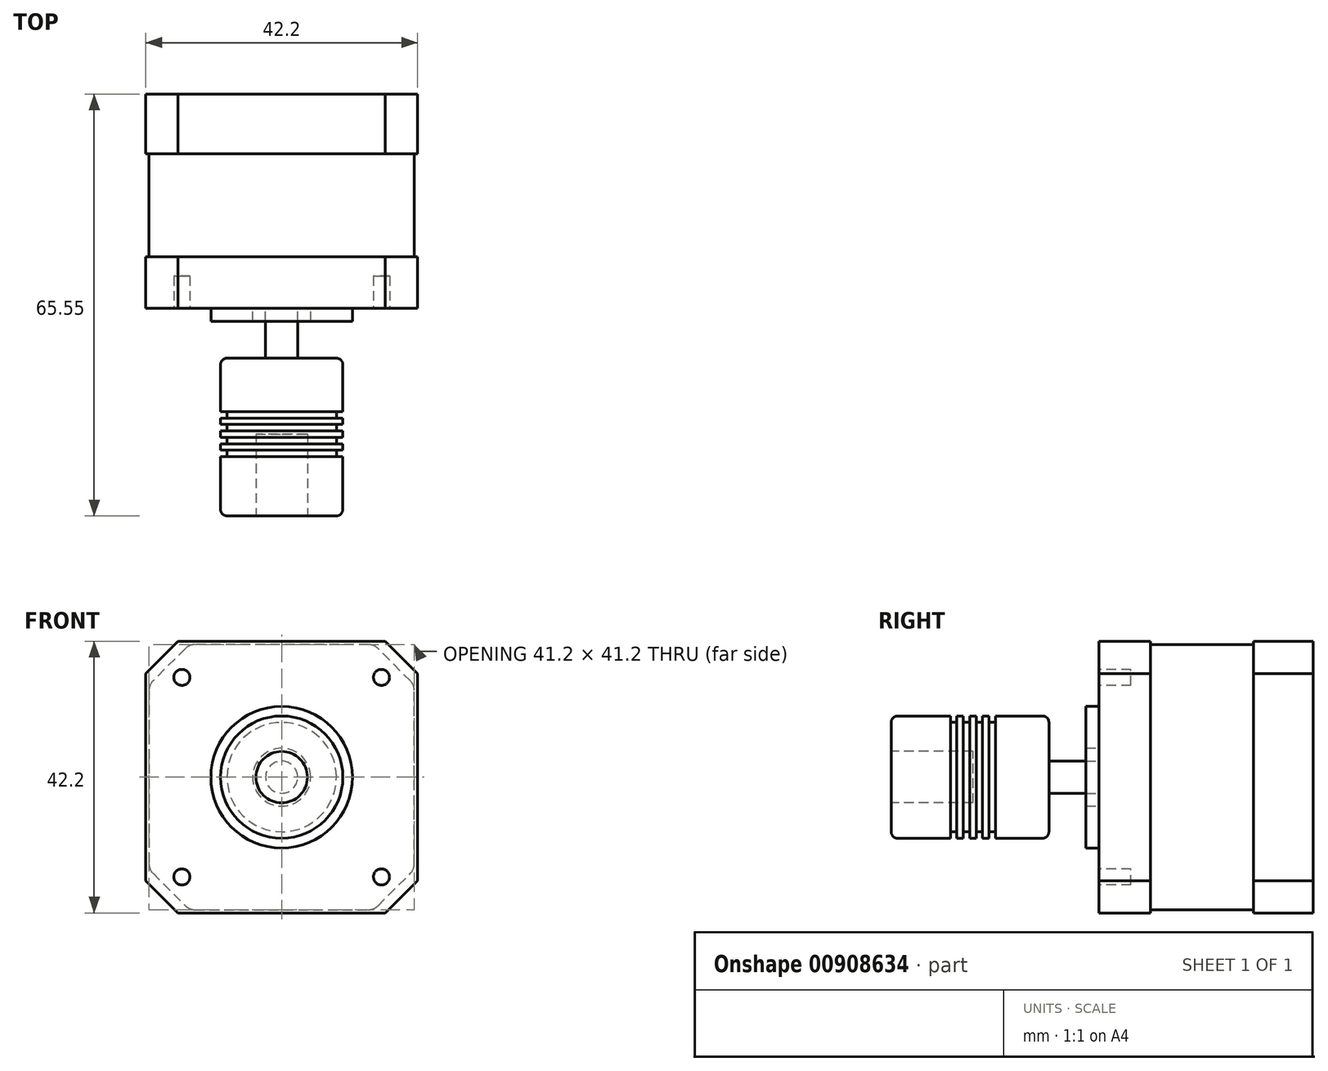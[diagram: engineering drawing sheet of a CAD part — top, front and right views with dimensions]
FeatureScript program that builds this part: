
annotation { "Feature Type Name" : "Feature", "Feature Type Description" : "" }
export const myFeature = defineFeature(function(context is Context, id is Id, definition is map)
    precondition{}
    {
        {
            var Q0;
            Q0=qCreatedBy(makeId("Front.planeOp"),FACE);
            var sketch = newSketch(context, id + "F0", { "sketchPlane" : qUnion([Q0])});
            skLineSegment(sketch, "E0.bottom", {"start": v(-21.1, 21.1) * mm, "end": v(21.1, 21.1) * mm});
            skLineSegment(sketch, "E0.top", {"start": v(-21.1, -21.1) * mm, "end": v(21.1, -21.1) * mm});
            skLineSegment(sketch, "E0.left", {"start": v(-21.1, 21.1) * mm, "end": v(-21.1, -21.1) * mm});
            skLineSegment(sketch, "E0.right", {"start": v(21.1, 21.1) * mm, "end": v(21.1, -21.1) * mm});
            skLineSegment(sketch, "E1", {"start": v(-21.1, 21.1) * mm, "end": v(21.1, -21.1) * mm, "construction": true});
            skCircle(sketch, "E2", {"center": v(0, 0) * mm, "radius": 2.5 * mm});
            skSolve(sketch);
        }
        {
            var Q0;
            Q0=makeQuery(id+"F0.imprint","IMPRINT",FACE,{"disambiguationData":[TD([[makeQuery(id+"F0.imprint","IMPRINT",EDGE,{"derivedFrom":sQuery(id+"F0.wireOp",EDGE,"E2")}),1.0]])]});
            var Q1;
            Q1=makeQuery(id+"F0.imprint","IMPRINT",FACE,{"disambiguationData":[TD([[makeQuery(id+"F0.imprint","IMPRINT",EDGE,{"derivedFrom":sQuery(id+"F0.wireOp",EDGE,"E0.bottom")}),-1.0]])]});
            extrude(context, id + "F1", {"entities" : qUnion([Q0, Q1]), "oppositeDirection" : true, "depth" : 33.3 * mm, "offsetDistance" : 25 * mm});
        }
        {
            var Q0;
            Q0=makeQuery(id+"F1.opExtrude","SWEPT_EDGE",EDGE,{"disambiguationData":[OSD([sQuery(id+"F0.wireOp",EDGE,"E0.bottom"),sQuery(id+"F0.wireOp",EDGE,"E0.right")])]});
            var Q1;
            Q1=makeQuery(id+"F1.opExtrude","SWEPT_EDGE",EDGE,{"disambiguationData":[OSD([sQuery(id+"F0.wireOp",EDGE,"E0.bottom"),sQuery(id+"F0.wireOp",EDGE,"E0.left")])]});
            var Q2;
            Q2=makeQuery(id+"F1.opExtrude","SWEPT_EDGE",EDGE,{"disambiguationData":[OSD([sQuery(id+"F0.wireOp",EDGE,"E0.top"),sQuery(id+"F0.wireOp",EDGE,"E0.right")])]});
            var Q3;
            Q3=makeQuery(id+"F1.opExtrude","SWEPT_EDGE",EDGE,{"disambiguationData":[OSD([sQuery(id+"F0.wireOp",EDGE,"E0.top"),sQuery(id+"F0.wireOp",EDGE,"E0.left")])]});
            chamfer(context, id + "F2", {"entities" : qUnion([Q0, Q1, Q2, Q3]), "width" : 5 * mm, "tangentPropagation" : true});
        }
        {
            var Q0;
            Q0=makeQuery(id+"F0.imprint","IMPRINT",FACE,{"disambiguationData":[TD([[makeQuery(id+"F0.imprint","IMPRINT",EDGE,{"derivedFrom":sQuery(id+"F0.wireOp",EDGE,"E2")}),1.0]])]});
            extrude(context, id + "F3", {"entities" : qUnion([Q0]), "operationType" : NewBodyOperationType.ADD, "depth" : 20 * mm, "offsetDistance" : 25 * mm});
        }
        {
            var Q0;
            Q0=makeQuery(id+"F1.opExtrude","CAP_FACE",FACE,{"disambiguationData":[OSD([sQuery(id+"F0.wireOp",EDGE,"E0.bottom"),sQuery(id+"F0.wireOp",EDGE,"E0.top"),sQuery(id+"F0.wireOp",EDGE,"E0.left"),sQuery(id+"F0.wireOp",EDGE,"E0.right")])],"isStart":true});
            var sketch = newSketch(context, id + "F4", { "sketchPlane" : qUnion([Q0])});
            skCircle(sketch, "E3", {"center": v(0, 0) * mm, "radius": 4.5 * mm});
            skCircle(sketch, "E4", {"center": v(0, 0) * mm, "radius": 11 * mm});
            skSolve(sketch);
        }
        {
            var Q0;
            Q0 = qSketchRegion(id + "F4", true);
            extrude(context, id + "F5", {"entities" : qUnion([Q0]), "operationType" : NewBodyOperationType.ADD, "depth" : 2 * mm, "offsetDistance" : 25 * mm});
        }
        {
            var Q0;
            {var subQ0=sQuery(id+"F0.wireOp",EDGE,"E0.left");var subQ1=sQuery(id+"F0.wireOp",EDGE,"E0.bottom");var subQ2=sQuery(id+"F0.wireOp",EDGE,"E0.top");var subQ3=sQuery(id+"F0.wireOp",EDGE,"E0.right");Q0=makeQuery(id+"F5.boolean.opBoolean","SPLIT",FACE,{"disambiguationData":[TD([makeQuery(id+"F1.opExtrude","SWEPT_FACE",FACE,{"disambiguationData":[OSD([subQ1])]})])],"derivedFrom":makeQuery(id+"F1.opExtrude","CAP_FACE",FACE,{"disambiguationData":[OSD([subQ1,subQ2,subQ0,subQ3])],"isStart":true})});}
            var sketch = newSketch(context, id + "F6", { "sketchPlane" : qUnion([Q0])});
            skCircle(sketch, "E5", {"center": v(-15.5, 15.5) * mm, "radius": 1.25 * mm});
            skCircle(sketch, "E6.1.0", {"center": v(-15.5, -15.5) * mm, "radius": 1.25 * mm});
            skCircle(sketch, "E6.2.0", {"center": v(15.5, -15.5) * mm, "radius": 1.25 * mm});
            skCircle(sketch, "E6.3.0", {"center": v(15.5, 15.5) * mm, "radius": 1.25 * mm});
            skPoint(sketch, "E6.center", {"position": v(0, 0) * mm});
            skSolve(sketch);
        }
        {
            var Q0;
            Q0 = qSketchRegion(id + "F6", true);
            extrude(context, id + "F7", {"entities" : qUnion([Q0]), "operationType" : NewBodyOperationType.REMOVE, "oppositeDirection" : true, "depth" : 5 * mm, "offsetDistance" : 25 * mm});
        }
        {
            var Q0;
            {var subQ0=sQuery(id+"F0.wireOp",EDGE,"E0.left");var subQ1=sQuery(id+"F0.wireOp",EDGE,"E0.bottom");var subQ2=sQuery(id+"F0.wireOp",EDGE,"E0.top");var subQ3=sQuery(id+"F0.wireOp",EDGE,"E0.right");Q0=makeQuery(id+"F5.boolean.opBoolean","SPLIT",FACE,{"disambiguationData":[TD([makeQuery(id+"F1.opExtrude","SWEPT_FACE",FACE,{"disambiguationData":[OSD([subQ1])]})])],"derivedFrom":makeQuery(id+"F1.opExtrude","CAP_FACE",FACE,{"disambiguationData":[OSD([subQ1,subQ2,subQ0,subQ3])],"isStart":true})});}
            cPlane(context, id + "F8", {"entities" : qUnion([Q0]), "cplaneType" : CPlaneType.OFFSET, "offset" : 8 * mm, "oppositeDirection" : true, "width" : 150 * mm, "height" : 150 * mm});
        }
        {
            var Q0;
            Q0=qCreatedBy(id+"F8.planeOp",FACE);
            var sketch = newSketch(context, id + "F9", { "sketchPlane" : qUnion([Q0])});
            skLineSegment(sketch, "E7", {"start": v(0, 0) * mm, "end": v(0, 20.6) * mm});
            skLineSegment(sketch, "E8", {"start": v(0, 20.6) * mm, "end": v(-14.34, 20.6) * mm});
            skLineSegment(sketch, "E9", {"start": v(-14.34, 20.6) * mm, "end": v(-20.6, 14.34) * mm});
            skLineSegment(sketch, "E10", {"start": v(-20.6, 14.34) * mm, "end": v(-20.6, 0) * mm});
            skLineSegment(sketch, "E11", {"start": v(-20.6, 0) * mm, "end": v(0, 0) * mm});
            skLineSegment(sketch, "E12.1.0", {"start": v(-20.6, 0) * mm, "end": v(-20.6, -14.34) * mm});
            skLineSegment(sketch, "E12.1.1", {"start": v(-14.34, -20.6) * mm, "end": v(0, -20.6) * mm});
            skLineSegment(sketch, "E12.1.2", {"start": v(-20.6, -14.34) * mm, "end": v(-14.34, -20.6) * mm});
            skLineSegment(sketch, "E12.2.0", {"start": v(0, -20.6) * mm, "end": v(14.34, -20.6) * mm});
            skLineSegment(sketch, "E12.2.1", {"start": v(20.6, -14.34) * mm, "end": v(20.6, 0) * mm});
            skLineSegment(sketch, "E12.2.2", {"start": v(14.34, -20.6) * mm, "end": v(20.6, -14.34) * mm});
            skLineSegment(sketch, "E12.3.0", {"start": v(20.6, 0) * mm, "end": v(20.6, 14.34) * mm});
            skLineSegment(sketch, "E12.3.1", {"start": v(14.34, 20.6) * mm, "end": v(0, 20.6) * mm});
            skLineSegment(sketch, "E12.3.2", {"start": v(20.6, 14.34) * mm, "end": v(14.34, 20.6) * mm});
            skPoint(sketch, "E12.center", {"position": v(0, 0) * mm});
            skLineSegment(sketch, "E13.bottom", {"start": v(-24.85, 25.17) * mm, "end": v(25.9, 25.17) * mm});
            skLineSegment(sketch, "E13.top", {"start": v(-24.85, -25.03) * mm, "end": v(25.9, -25.03) * mm});
            skLineSegment(sketch, "E13.left", {"start": v(-24.85, 25.17) * mm, "end": v(-24.85, -25.03) * mm});
            skLineSegment(sketch, "E13.right", {"start": v(25.9, 25.17) * mm, "end": v(25.9, -25.03) * mm});
            skSolve(sketch);
        }
        {
            var Q0;
            Q0 = qSketchRegion(id + "F9", true);
            extrude(context, id + "F10", {"entities" : qUnion([Q0]), "operationType" : NewBodyOperationType.REMOVE, "oppositeDirection" : true, "depth" : 16 * mm, "offsetDistance" : 25 * mm});
        }
        {
            var Q0;
            Q0=makeQuery(id+"F10.boolean.opBoolean","COPY",EDGE,{"derivedFrom":makeQuery(id+"F10.opExtrude","SWEPT_EDGE",EDGE,{"disambiguationData":[OSD([sQuery(id+"F9.wireOp",EDGE,"E12.3.0"),sQuery(id+"F9.wireOp",EDGE,"E12.3.2")])]})});
            var Q1;
            Q1=makeQuery(id+"F10.boolean.opBoolean","COPY",EDGE,{"derivedFrom":makeQuery(id+"F10.opExtrude","SWEPT_EDGE",EDGE,{"disambiguationData":[OSD([sQuery(id+"F9.wireOp",EDGE,"E12.3.1"),sQuery(id+"F9.wireOp",EDGE,"E12.3.2")])]})});
            var Q2;
            Q2=makeQuery(id+"F10.boolean.opBoolean","COPY",EDGE,{"derivedFrom":makeQuery(id+"F10.opExtrude","SWEPT_EDGE",EDGE,{"disambiguationData":[OSD([sQuery(id+"F9.wireOp",EDGE,"E8"),sQuery(id+"F9.wireOp",EDGE,"E9")])]})});
            var Q3;
            Q3=makeQuery(id+"F10.boolean.opBoolean","COPY",EDGE,{"derivedFrom":makeQuery(id+"F10.opExtrude","SWEPT_EDGE",EDGE,{"disambiguationData":[OSD([sQuery(id+"F9.wireOp",EDGE,"E9"),sQuery(id+"F9.wireOp",EDGE,"E10")])]})});
            var Q4;
            Q4=makeQuery(id+"F10.boolean.opBoolean","COPY",EDGE,{"derivedFrom":makeQuery(id+"F10.opExtrude","SWEPT_EDGE",EDGE,{"disambiguationData":[OSD([sQuery(id+"F9.wireOp",EDGE,"E12.1.0"),sQuery(id+"F9.wireOp",EDGE,"E12.1.2")])]})});
            var Q5;
            Q5=makeQuery(id+"F10.boolean.opBoolean","COPY",EDGE,{"derivedFrom":makeQuery(id+"F10.opExtrude","SWEPT_EDGE",EDGE,{"disambiguationData":[OSD([sQuery(id+"F9.wireOp",EDGE,"E12.1.1"),sQuery(id+"F9.wireOp",EDGE,"E12.1.2")])]})});
            var Q6;
            Q6=makeQuery(id+"F10.boolean.opBoolean","COPY",EDGE,{"derivedFrom":makeQuery(id+"F10.opExtrude","SWEPT_EDGE",EDGE,{"disambiguationData":[OSD([sQuery(id+"F9.wireOp",EDGE,"E12.2.1"),sQuery(id+"F9.wireOp",EDGE,"E12.2.2")])]})});
            var Q7;
            Q7=makeQuery(id+"F10.boolean.opBoolean","COPY",EDGE,{"derivedFrom":makeQuery(id+"F10.opExtrude","SWEPT_EDGE",EDGE,{"disambiguationData":[OSD([sQuery(id+"F9.wireOp",EDGE,"E12.2.0"),sQuery(id+"F9.wireOp",EDGE,"E12.2.2")])]})});
            fillet(context, id + "F11", {"entities" : qUnion([Q0, Q1, Q2, Q3, Q4, Q5, Q6, Q7]), "radius" : 2 * mm, "tangentPropagation" : true, "allowEdgeOverflow" : false});
        }
        {
            var Q0;
            Q0=makeQuery(id+"F3.opExtrude","CAP_FACE",FACE,{"disambiguationData":[OSD([sQuery(id+"F0.wireOp",EDGE,"E2")])],"isStart":false});
            var sketch = newSketch(context, id + "F12", { "sketchPlane" : qUnion([Q0])});
            skCircle(sketch, "E14", {"center": v(0, 0) * mm, "radius": 9.5 * mm});
            skSolve(sketch);
        }
        {
            var Q0;
            Q0 = qSketchRegion(id + "F12", true);
            extrude(context, id + "F13", {"entities" : qUnion([Q0]), "operationType" : NewBodyOperationType.ADD, "endBound" : BoundingType.SYMMETRIC, "depth" : 24.5 * mm, "offsetDistance" : 25 * mm});
        }
        {
            var Q0;
            Q0=makeQuery(id+"F13.opExtrude","CAP_FACE",FACE,{"disambiguationData":[OSD([sQuery(id+"F12.wireOp",EDGE,"E14")])],"isStart":false});
            var sketch = newSketch(context, id + "F14", { "sketchPlane" : qUnion([Q0])});
            skCircle(sketch, "E15", {"center": v(0, 0) * mm, "radius": 4 * mm});
            skSolve(sketch);
        }
        {
            var Q0;
            Q0 = qSketchRegion(id + "F14", true);
            extrude(context, id + "F15", {"entities" : qUnion([Q0]), "operationType" : NewBodyOperationType.REMOVE, "oppositeDirection" : true, "depth" : (25.4 / 2) * mm, "offsetDistance" : 25 * mm});
        }
        {
            var Q0;
            Q0=makeQuery(id+"F13.opExtrude","CAP_EDGE",EDGE,{"disambiguationData":[OSD([sQuery(id+"F12.wireOp",EDGE,"E14")])],"isStart":false});
            var Q1;
            Q1=makeQuery(id+"F13.opExtrude","CAP_EDGE",EDGE,{"disambiguationData":[OSD([sQuery(id+"F12.wireOp",EDGE,"E14")])],"isStart":true});
            var Q2;
            Q2=makeQuery(id+"F15.boolean.opBoolean","COPY",EDGE,{"derivedFrom":makeQuery(id+"F15.opExtrude","CAP_EDGE",EDGE,{"disambiguationData":[OSD([sQuery(id+"F14.wireOp",EDGE,"E15")])],"isStart":true})});
            fillet(context, id + "F16", {"entities" : qUnion([Q0, Q1, Q2]), "radius" : 1 * mm, "tangentPropagation" : true, "allowEdgeOverflow" : false});
        }
        {
            var Q0;
            Q0=qCreatedBy(makeId("Right.planeOp"),FACE);
            var sketch = newSketch(context, id + "F17", { "sketchPlane" : qUnion([Q0])});
            skLineSegment(sketch, "E16", {"start": v(-19.55, 17.45) * mm, "end": v(-19.55, -14.9) * mm, "construction": true});
            skLineSegment(sketch, "E17.0", {"start": v(-19.55, -4) * mm, "end": v(-19.55, 4) * mm, "construction": true});
            skLineSegment(sketch, "E18", {"start": v(-31.25, 9.5) * mm, "end": v(-8.75, 9.5) * mm});
            skLineSegment(sketch, "E19.bottom", {"start": v(-20.05, 9.5) * mm, "end": v(-21.05, 9.5) * mm});
            skLineSegment(sketch, "E19.top", {"start": v(-20.05, 8.5) * mm, "end": v(-21.05, 8.5) * mm});
            skLineSegment(sketch, "E19.left", {"start": v(-20.05, 9.5) * mm, "end": v(-20.05, 8.5) * mm});
            skLineSegment(sketch, "E19.right", {"start": v(-21.05, 9.5) * mm, "end": v(-21.05, 8.5) * mm});
            skLineSegment(sketch, "E20.bottom", {"start": v(-22.05, 9.5) * mm, "end": v(-23.05, 9.5) * mm});
            skLineSegment(sketch, "E20.top", {"start": v(-22.05, 8.5) * mm, "end": v(-23.05, 8.5) * mm});
            skLineSegment(sketch, "E20.left", {"start": v(-22.05, 9.5) * mm, "end": v(-22.05, 8.5) * mm});
            skLineSegment(sketch, "E20.right", {"start": v(-23.05, 9.5) * mm, "end": v(-23.05, 8.5) * mm});
            skLineSegment(sketch, "E21.bottom", {"start": v(-19.05, 9.5) * mm, "end": v(-18.05, 9.5) * mm});
            skLineSegment(sketch, "E21.top", {"start": v(-19.05, 8.5) * mm, "end": v(-18.05, 8.5) * mm});
            skLineSegment(sketch, "E21.left", {"start": v(-19.05, 9.5) * mm, "end": v(-19.05, 8.5) * mm});
            skLineSegment(sketch, "E21.right", {"start": v(-18.05, 9.5) * mm, "end": v(-18.05, 8.5) * mm});
            skLineSegment(sketch, "E22.bottom", {"start": v(-17.05, 9.5) * mm, "end": v(-16.05, 9.5) * mm});
            skLineSegment(sketch, "E22.top", {"start": v(-17.05, 8.5) * mm, "end": v(-16.05, 8.5) * mm});
            skLineSegment(sketch, "E22.left", {"start": v(-17.05, 9.5) * mm, "end": v(-17.05, 8.5) * mm});
            skLineSegment(sketch, "E22.right", {"start": v(-16.05, 9.5) * mm, "end": v(-16.05, 8.5) * mm});
            skLineSegment(sketch, "E23", {"start": v(-19.05, 8.5) * mm, "end": v(-20.05, 8.5) * mm, "construction": true});
            skPoint(sketch, "E24", {"position": v(-19.55, 8.5) * mm});
            skLineSegment(sketch, "E25", {"start": v(-22.05, 8.5) * mm, "end": v(-21.05, 8.5) * mm, "construction": true});
            skLineSegment(sketch, "E26", {"start": v(-18.05, 8.5) * mm, "end": v(-17.05, 8.5) * mm, "construction": true});
            skLineSegment(sketch, "E27", {"start": v(-35.6, 0) * mm, "end": v(18.11, 0) * mm, "construction": true});
            skSolve(sketch);
        }
        {
            var Q0;
            Q0 = qSketchRegion(id + "F17", true);
            var Q1;
            Q1=sQuery(id+"F17.wireOp",EDGE,"E27");
            revolve(context, id + "F18", {"operationType" : NewBodyOperationType.REMOVE, "surfaceOperationType" : NewSurfaceOperationType.NEW, "entities" : qUnion([Q0]), "axis" : qUnion([Q1]), "revolveType" : RevolveType.FULL, "oppositeDirection" : true});
        }
    });
